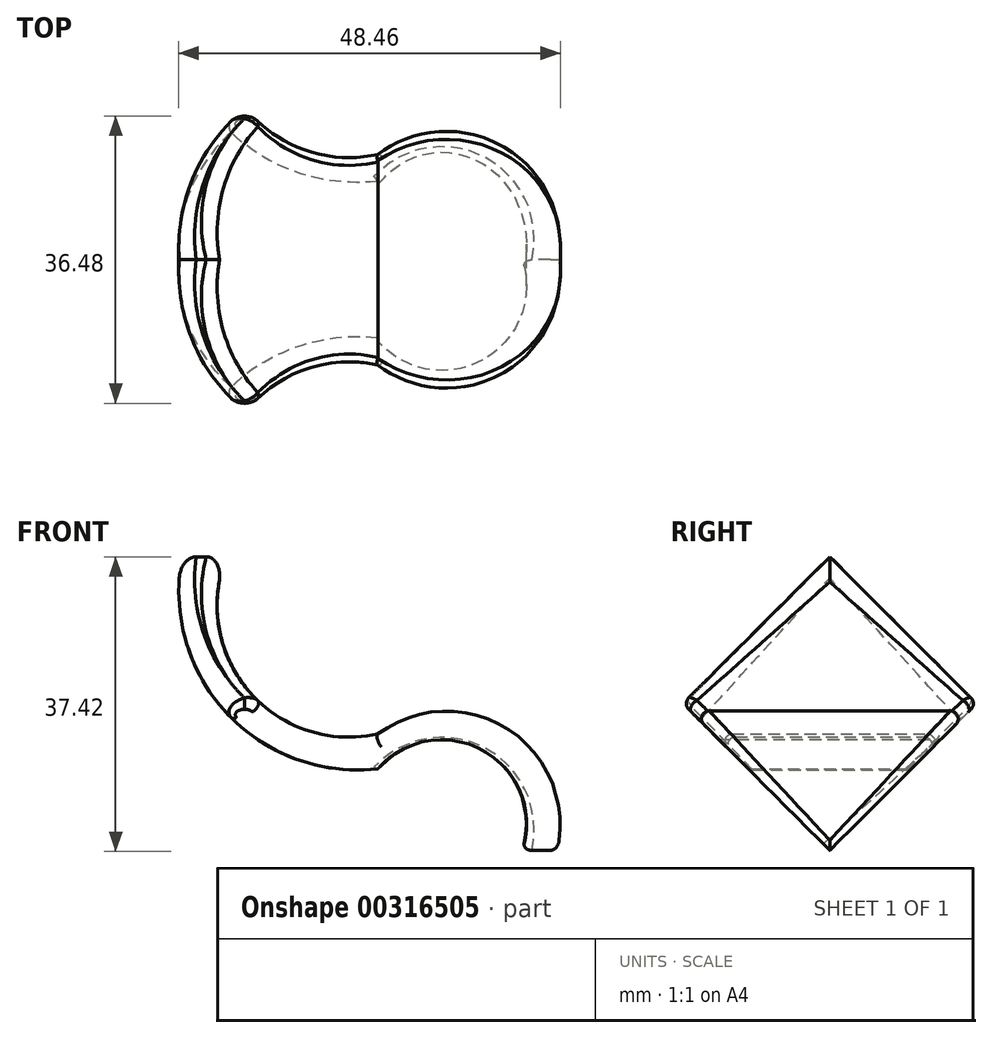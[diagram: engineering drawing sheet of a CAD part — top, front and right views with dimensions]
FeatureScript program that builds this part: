
annotation { "Feature Type Name" : "Feature", "Feature Type Description" : "" }
export const myFeature = defineFeature(function(context is Context, id is Id, definition is map)
    precondition{}
    {
        {
            var Q0;
            Q0=qCreatedBy(makeId("Front.planeOp"),FACE);
            var sketch = newSketch(context, id + "F0", { "sketchPlane" : qUnion([Q0])});
            skArc(sketch, "E0", {"start": v(-74.9, 37.3) * mm, "mid": v(-72.07, 20.24) * mm, "end": v(-55.66, 14.8) * mm});
            skArc(sketch, "E1", {"start": v(-32.86, 0) * mm, "mid": v(-39.08, 15.39) * mm, "end": v(-55.66, 14.8) * mm});
            skArc(sketch, "E2", {"start": v(-80.53, 37.3) * mm, "mid": v(-74.93, 17.52) * mm, "end": v(-55.66, 10.36) * mm});
            skArc(sketch, "E3", {"start": v(-37.3, 0) * mm, "mid": v(-42.23, 12.7) * mm, "end": v(-55.66, 10.36) * mm});
            skLineSegment(sketch, "E4", {"start": v(-74.9, 37.3) * mm, "end": v(-80.53, 37.3) * mm});
            skLineSegment(sketch, "E5", {"start": v(-37.3, 0) * mm, "end": v(-32.86, 0) * mm});
            skSolve(sketch);
        }
        {
            var Q0;
            Q0=makeQuery(id+"F0.imprint","IMPRINT",FACE,{"disambiguationData":[TD([[makeQuery(id+"F0.imprint","IMPRINT",EDGE,{"derivedFrom":sQuery(id+"F0.wireOp",EDGE,"E0")}),-1.0]])]});
            extrude(context, id + "F1", {"entities" : qUnion([Q0]), "depth" : 40 * mm});
        }
        {
            var Q0;
            Q0=makeQuery(id+"F1.opExtrude","CAP_EDGE",EDGE,{"disambiguationData":[OSD([sQuery(id+"F0.wireOp",EDGE,"E4")])],"isStart":false});
            var Q1;
            Q1=makeQuery(id+"F1.opExtrude","CAP_EDGE",EDGE,{"disambiguationData":[OSD([sQuery(id+"F0.wireOp",EDGE,"E4")])],"isStart":true});
            var Q2;
            Q2=makeQuery(id+"F1.opExtrude","CAP_EDGE",EDGE,{"disambiguationData":[OSD([sQuery(id+"F0.wireOp",EDGE,"E5")])],"isStart":false});
            var Q3;
            Q3=makeQuery(id+"F1.opExtrude","CAP_EDGE",EDGE,{"disambiguationData":[OSD([sQuery(id+"F0.wireOp",EDGE,"E5")])],"isStart":true});
            chamfer(context, id + "F2", {"entities" : qUnion([Q0, Q1, Q2, Q3]), "width" : 20 * mm, "tangentPropagation" : true});
        }
        {
            var Q0;
            Q0=makeQuery(id+"F2.opChamfer","BLEND_EDGE",EDGE,{"blendedFrom":[makeQuery(id+"F1.opExtrude","CAP_EDGE",EDGE,{"disambiguationData":[OSD([sQuery(id+"F0.wireOp",EDGE,"E4")])],"isStart":false}),makeQuery(id+"F1.opExtrude","SWEPT_FACE",FACE,{"disambiguationData":[OSD([sQuery(id+"F0.wireOp",EDGE,"E2")])]})],"blendedInto":[makeQuery(id+"F1.opExtrude","SWEPT_FACE",FACE,{"disambiguationData":[OSD([sQuery(id+"F0.wireOp",EDGE,"E2")])]})]});
            var Q1;
            Q1=makeQuery(id+"F2.opChamfer","BLEND_EDGE",EDGE,{"blendedFrom":[makeQuery(id+"F1.opExtrude","CAP_EDGE",EDGE,{"disambiguationData":[OSD([sQuery(id+"F0.wireOp",EDGE,"E4")])],"isStart":false}),makeQuery(id+"F1.opExtrude","SWEPT_FACE",FACE,{"disambiguationData":[OSD([sQuery(id+"F0.wireOp",EDGE,"E0")])]})],"blendedInto":[makeQuery(id+"F1.opExtrude","SWEPT_FACE",FACE,{"disambiguationData":[OSD([sQuery(id+"F0.wireOp",EDGE,"E0")])]})]});
            var Q2;
            Q2=makeQuery(id+"F2.opChamfer","BLEND_EDGE",EDGE,{"blendedFrom":[makeQuery(id+"F1.opExtrude","CAP_EDGE",EDGE,{"disambiguationData":[OSD([sQuery(id+"F0.wireOp",EDGE,"E4")])],"isStart":true}),makeQuery(id+"F1.opExtrude","SWEPT_FACE",FACE,{"disambiguationData":[OSD([sQuery(id+"F0.wireOp",EDGE,"E0")])]})],"blendedInto":[makeQuery(id+"F1.opExtrude","SWEPT_FACE",FACE,{"disambiguationData":[OSD([sQuery(id+"F0.wireOp",EDGE,"E0")])]})]});
            var Q3;
            Q3=makeQuery(id+"F2.opChamfer","BLEND_EDGE",EDGE,{"blendedFrom":[makeQuery(id+"F1.opExtrude","CAP_EDGE",EDGE,{"disambiguationData":[OSD([sQuery(id+"F0.wireOp",EDGE,"E4")])],"isStart":true}),makeQuery(id+"F1.opExtrude","SWEPT_FACE",FACE,{"disambiguationData":[OSD([sQuery(id+"F0.wireOp",EDGE,"E2")])]})],"blendedInto":[makeQuery(id+"F1.opExtrude","SWEPT_FACE",FACE,{"disambiguationData":[OSD([sQuery(id+"F0.wireOp",EDGE,"E2")])]})]});
            fillet(context, id + "F3", {"entities" : qUnion([Q0, Q1, Q2, Q3]), "tangentPropagation" : true, "radius" : 2 * mm, "defaultsChanged" : false, "vertexSettings" : [], "allowEdgeOverflow" : false});
        }
        {
            var Q0;
            Q0=makeQuery(id+"F2.opChamfer","BLEND_EDGE",EDGE,{"blendedFrom":[makeQuery(id+"F1.opExtrude","CAP_EDGE",EDGE,{"disambiguationData":[OSD([sQuery(id+"F0.wireOp",EDGE,"E5")])],"isStart":true}),makeQuery(id+"F1.opExtrude","SWEPT_FACE",FACE,{"disambiguationData":[OSD([sQuery(id+"F0.wireOp",EDGE,"E0")])]})],"blendedInto":[makeQuery(id+"F1.opExtrude","SWEPT_FACE",FACE,{"disambiguationData":[OSD([sQuery(id+"F0.wireOp",EDGE,"E0")])]})]});
            var Q1;
            Q1=makeQuery(id+"F2.opChamfer","BLEND_EDGE",EDGE,{"blendedFrom":[makeQuery(id+"F1.opExtrude","CAP_EDGE",EDGE,{"disambiguationData":[OSD([sQuery(id+"F0.wireOp",EDGE,"E5")])],"isStart":true}),makeQuery(id+"F1.opExtrude","SWEPT_FACE",FACE,{"disambiguationData":[OSD([sQuery(id+"F0.wireOp",EDGE,"E1")])]})],"blendedInto":[makeQuery(id+"F1.opExtrude","SWEPT_FACE",FACE,{"disambiguationData":[OSD([sQuery(id+"F0.wireOp",EDGE,"E1")])]})]});
            var Q2;
            Q2=makeQuery(id+"F2.opChamfer","BLEND_EDGE",EDGE,{"blendedFrom":[makeQuery(id+"F1.opExtrude","CAP_EDGE",EDGE,{"disambiguationData":[OSD([sQuery(id+"F0.wireOp",EDGE,"E5")])],"isStart":true}),makeQuery(id+"F1.opExtrude","SWEPT_FACE",FACE,{"disambiguationData":[OSD([sQuery(id+"F0.wireOp",EDGE,"E3")])]})],"blendedInto":[makeQuery(id+"F1.opExtrude","SWEPT_FACE",FACE,{"disambiguationData":[OSD([sQuery(id+"F0.wireOp",EDGE,"E3")])]})]});
            var Q3;
            Q3=makeQuery(id+"F2.opChamfer","BLEND_EDGE",EDGE,{"blendedFrom":[makeQuery(id+"F1.opExtrude","CAP_EDGE",EDGE,{"disambiguationData":[OSD([sQuery(id+"F0.wireOp",EDGE,"E5")])],"isStart":true}),makeQuery(id+"F1.opExtrude","SWEPT_FACE",FACE,{"disambiguationData":[OSD([sQuery(id+"F0.wireOp",EDGE,"E2")])]})],"blendedInto":[makeQuery(id+"F1.opExtrude","SWEPT_FACE",FACE,{"disambiguationData":[OSD([sQuery(id+"F0.wireOp",EDGE,"E2")])]})]});
            var Q4;
            Q4=makeQuery(id+"F2.opChamfer","BLEND_EDGE",EDGE,{"blendedFrom":[makeQuery(id+"F1.opExtrude","CAP_EDGE",EDGE,{"disambiguationData":[OSD([sQuery(id+"F0.wireOp",EDGE,"E5")])],"isStart":false}),makeQuery(id+"F1.opExtrude","SWEPT_FACE",FACE,{"disambiguationData":[OSD([sQuery(id+"F0.wireOp",EDGE,"E0")])]})],"blendedInto":[makeQuery(id+"F1.opExtrude","SWEPT_FACE",FACE,{"disambiguationData":[OSD([sQuery(id+"F0.wireOp",EDGE,"E0")])]})]});
            var Q5;
            Q5=makeQuery(id+"F2.opChamfer","BLEND_EDGE",EDGE,{"blendedFrom":[makeQuery(id+"F1.opExtrude","CAP_EDGE",EDGE,{"disambiguationData":[OSD([sQuery(id+"F0.wireOp",EDGE,"E5")])],"isStart":false}),makeQuery(id+"F1.opExtrude","SWEPT_FACE",FACE,{"disambiguationData":[OSD([sQuery(id+"F0.wireOp",EDGE,"E2")])]})],"blendedInto":[makeQuery(id+"F1.opExtrude","SWEPT_FACE",FACE,{"disambiguationData":[OSD([sQuery(id+"F0.wireOp",EDGE,"E2")])]})]});
            var Q6;
            Q6=makeQuery(id+"F2.opChamfer","BLEND_EDGE",EDGE,{"blendedFrom":[makeQuery(id+"F1.opExtrude","CAP_EDGE",EDGE,{"disambiguationData":[OSD([sQuery(id+"F0.wireOp",EDGE,"E5")])],"isStart":false}),makeQuery(id+"F1.opExtrude","SWEPT_FACE",FACE,{"disambiguationData":[OSD([sQuery(id+"F0.wireOp",EDGE,"E1")])]})],"blendedInto":[makeQuery(id+"F1.opExtrude","SWEPT_FACE",FACE,{"disambiguationData":[OSD([sQuery(id+"F0.wireOp",EDGE,"E1")])]})]});
            fillet(context, id + "F4", {"entities" : qUnion([Q0, Q1, Q2, Q3, Q4, Q5, Q6]), "tangentPropagation" : true, "radius" : 1 * mm, "defaultsChanged" : false, "vertexSettings" : [], "allowEdgeOverflow" : false});
        }
    });
